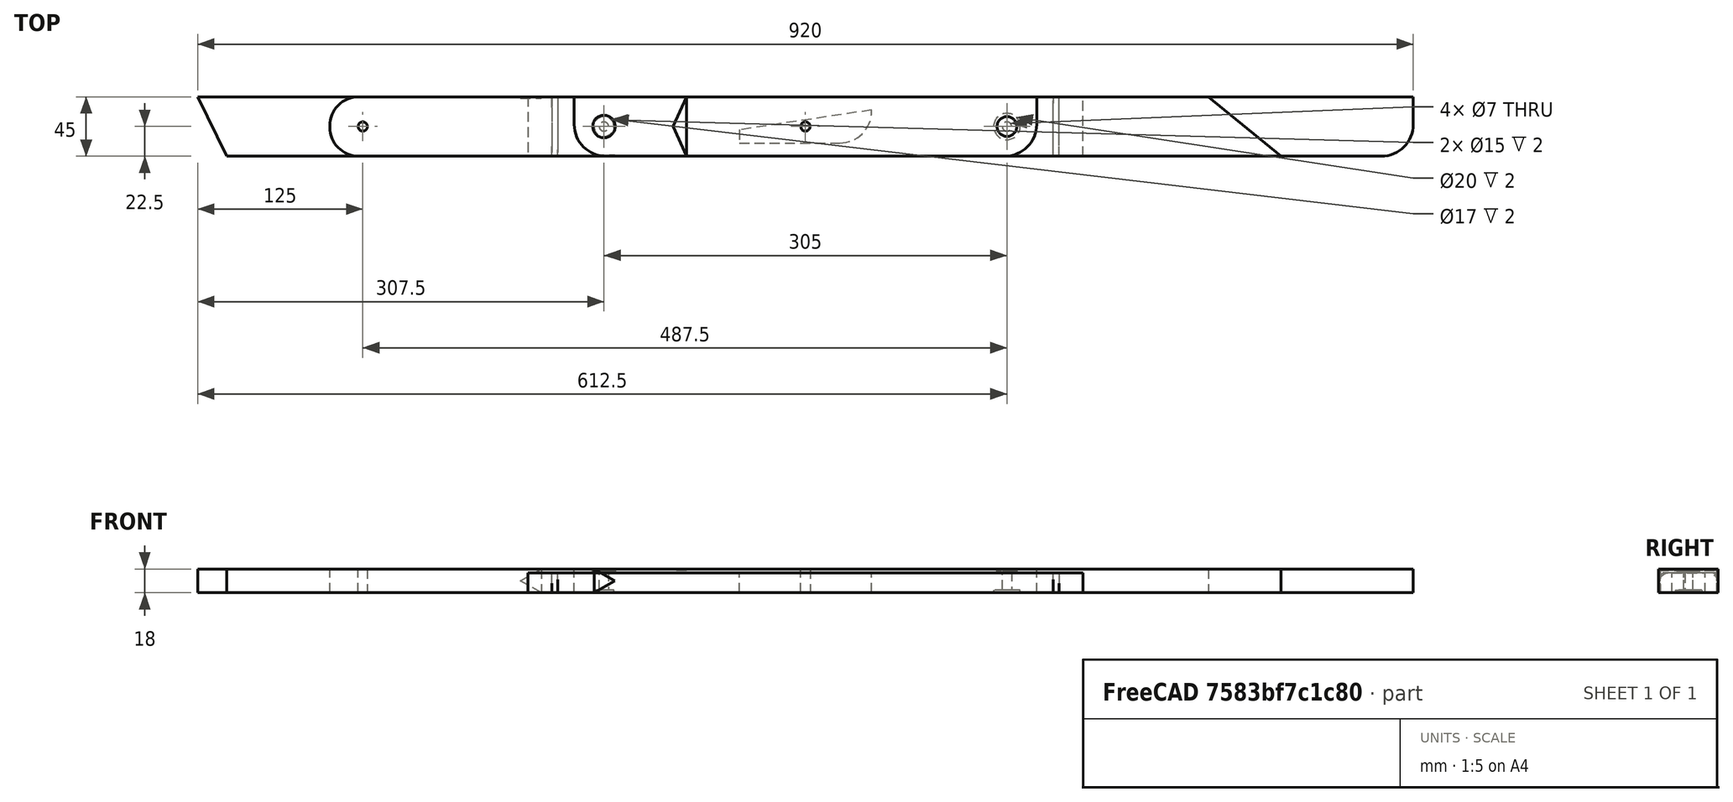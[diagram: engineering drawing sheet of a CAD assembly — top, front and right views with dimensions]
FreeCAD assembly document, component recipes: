
FREECAD ASSEMBLY — COMPONENT RECIPES ("wooden folding chair")

This assembly document has 20 components, labeled P0..P19 below (a component is one placed body or linked part). 20 of them carry a construction recipe — the FreeCAD feature program that regenerates the part from scratch, quoted from this document or its linked companion documents; the rest are supplied as boundary geometry only. No exploded tour is included for this assembly.
COMPONENT P0 — recipe-attached ("35 X 4,5 X 1,8 (1)", modeled in this document).
Construction recipe (the document's own serialized feature program — sketch geometry with constraints, then the solid features built on it; lengths are millimeters unless a unit is written):

FEATURE [Sketcher::SketchObject] Sketch
  FullyConstrained = true
  MapMode = 5
  Support = -> [XY_Plane]
  sketch-geometry (5):
    g0: LineSegment StartX=-175 StartY=22.5 StartZ=0 EndX=-175 EndY=-22.5 EndZ=0
    g1: LineSegment StartX=-175 StartY=-22.5 StartZ=0 EndX=175 EndY=-22.5 EndZ=0
    g2: LineSegment StartX=175 StartY=-22.5 StartZ=0 EndX=175 EndY=22.5 EndZ=0
    g3: LineSegment StartX=175 StartY=22.5 StartZ=0 EndX=-175 EndY=22.5 EndZ=0
    g4: GeomPoint X=0 Y=0 Z=0
  constraints (12):
    c: Coincident(g0,g1)
    c: Coincident(g1,g2)
    c: Coincident(g2,g3)
    c: Coincident(g3,g0)
    c: Horizontal(g1)
    c: Horizontal(g3)
    c: Vertical(g0)
    c: Vertical(g2)
    c: Symmetric(g1,g0,g4)
    c: Coincident(g4,g-1)
    c: DistanceY(g0,g0) = 45
    c: DistanceX(g3,g3) = 350
FEATURE [PartDesign::Pad] Pad
  Direction = (0,0,1)
  Length = 18
  Length2 = 10
  Profile = -> Sketch
  ReferenceAxis = -> Sketch [N_Axis]
  Type = 0
FEATURE [Sketcher::SketchObject] Sketch001
  ExternalGeometry = -> [Pad]
  FullyConstrained = true
  MapMode = 5
  Placement = pos=(0,0,18) rot=(0,0,1;0rad)
  Support = -> [Pad]
  sketch-geometry (2):
    g0: Circle CenterX=-152.5 CenterY=0 CenterZ=0 NormalX=0 NormalY=0 NormalZ=1 AngleXU=0 Radius=3.5
    g1: Circle CenterX=-152.5 CenterY=0 CenterZ=0 NormalX=0 NormalY=0 NormalZ=1 AngleXU=0 Radius=8.5
  constraints (5):
    c: PointOnObject(g0,g-1)
    c: Diameter(g0) = 7
    c: DistanceX(g-3,g0) = 22.5
    c: Coincident(g1,g0)
    c: Diameter(g1) = 17
FEATURE [PartDesign::Pocket] Pocket
  BaseFeature = -> Pad
  Direction = (0,0,-1)
  Length = 2
  Length2 = 5
  Profile = -> Sketch001
  ReferenceAxis = -> Sketch001 [N_Axis]
  Type = 0
FEATURE [PartDesign::Pocket] Pocket001
  BaseFeature = -> Pocket
  Direction = (0,0,-1)
  Length = 5
  Length2 = 5
  Profile = -> Pocket [Edge18]
  Type = 1
FEATURE [PartDesign::LinearPattern] LinearPattern
  BaseFeature = -> Pocket001
  Direction = -> X_Axis
  Length = 305
  Occurrences = 2
  Originals = -> [Pocket001]
FEATURE [Sketcher::SketchObject] Sketch002
  ExternalGeometry = -> [LinearPattern]
  FullyConstrained = true
  MapMode = 5
  Placement = pos=(0,0,0) rot=(1,0,0;3.14159rad)
  Support = -> [LinearPattern]
  sketch-geometry (1):
    g0: Circle CenterX=152.5 CenterY=0 CenterZ=0 NormalX=0 NormalY=0 NormalZ=1 AngleXU=0 Radius=10
  constraints (2):
    c: Coincident(g0,g-3)
    c: Diameter(g0) = 20
FEATURE [PartDesign::Pocket] Pocket002
  BaseFeature = -> LinearPattern
  Direction = (0,0,1)
  Length = 2
  Length2 = 5
  Profile = -> Sketch002
  ReferenceAxis = -> Sketch002 [N_Axis]
  Type = 0
FEATURE [PartDesign::Fillet] Fillet
  Base = -> Pocket002 [Edge2,Edge8]
  BaseFeature = -> Pocket002
  Radius = 24
  SupportTransform = false
  UseAllEdges = false
FEATURE [Sketcher::SketchObject] Sketch003
  ExternalGeometry = -> [Fillet]
  FullyConstrained = true
  MapMode = 5
  Placement = pos=(0,0,18) rot=(0,0,1;0rad)
  Support = -> [Fillet]
  sketch-geometry (1):
    g0: Circle CenterX=152.5 CenterY=0 CenterZ=0 NormalX=0 NormalY=0 NormalZ=1 AngleXU=0 Radius=7.5
  constraints (2):
    c: Coincident(g0,g-3)
    c: Diameter(g0) = 15
FEATURE [PartDesign::Pocket] Pocket003
  BaseFeature = -> Fillet
  Direction = (0,0,-1)
  Length = 2
  Length2 = 5
  Profile = -> Sketch003
  ReferenceAxis = -> Sketch003 [N_Axis]
  Type = 0
FEATURE [Sketcher::SketchObject] Sketch004
  ExternalGeometry = -> [Pocket003]
  FullyConstrained = true
  MapMode = 5
  Placement = pos=(0,0,0) rot=(1,0,0;3.14159rad)
  Support = -> [Pocket003]
  sketch-geometry (1):
    g0: Circle CenterX=-152.5 CenterY=0 CenterZ=0 NormalX=0 NormalY=0 NormalZ=1 AngleXU=0 Radius=7.5
  constraints (2):
    c: Coincident(g0,g-3)
    c: Diameter(g0) = 15
FEATURE [PartDesign::Pocket] Pocket004
  BaseFeature = -> Pocket003
  Direction = (0,0,1)
  Length = 2
  Length2 = 5
  Profile = -> Sketch004
  ReferenceAxis = -> Sketch004 [N_Axis]
  Type = 0
FEATURE [PartDesign::Body] Body  label="35 x 4,5 x 1,8"
  Group = -> [Sketch,Pad,Sketch001,Pocket,Pocket001,LinearPattern,Sketch002,Pocket002,Fillet,Sketch003,Pocket003,Sketch004,Pocket004]
  Origin = -> Origin
  Tip = -> Pocket004
COMPONENT P1 — recipe-attached ("37,5 X 4,5 X 1,5 (1)", modeled in this document).
Construction recipe (the document's own serialized feature program — sketch geometry with constraints, then the solid features built on it; lengths are millimeters unless a unit is written):

FEATURE [Sketcher::SketchObject] Sketch005
  FullyConstrained = true
  MapMode = 5
  Support = -> [XY_Plane001]
  sketch-geometry (5):
    g0: LineSegment StartX=-187.5 StartY=22.5 StartZ=0 EndX=-187.5 EndY=-22.5 EndZ=0
    g1: LineSegment StartX=-187.5 StartY=-22.5 StartZ=0 EndX=187.5 EndY=-22.5 EndZ=0
    g2: LineSegment StartX=187.5 StartY=-22.5 StartZ=0 EndX=187.5 EndY=22.5 EndZ=0
    g3: LineSegment StartX=187.5 StartY=22.5 StartZ=0 EndX=-187.5 EndY=22.5 EndZ=0
    g4: GeomPoint X=0 Y=0 Z=0
  constraints (12):
    c: Coincident(g0,g1)
    c: Coincident(g1,g2)
    c: Coincident(g2,g3)
    c: Coincident(g3,g0)
    c: Horizontal(g1)
    c: Horizontal(g3)
    c: Vertical(g0)
    c: Vertical(g2)
    c: Symmetric(g1,g0,g4)
    c: Coincident(g4,g-1)
    c: DistanceY(g0,g0) = 45
    c: DistanceX(g3,g3) = 375
FEATURE [PartDesign::Pad] Pad001
  Direction = (0,0,1)
  Length = 15
  Length2 = 10
  Profile = -> Sketch005
  ReferenceAxis = -> Sketch005 [N_Axis]
  Type = 0
FEATURE [PartDesign::Fillet] Fillet001
  Base = -> Pad001 [Edge7,Edge12]
  BaseFeature = -> Pad001
  Radius = 5
  SupportTransform = false
  UseAllEdges = false
FEATURE [PartDesign::Body] Body001  label="37,5 x 4,5 x 1,5"
  Group = -> [Sketch005,Pad001,Fillet001]
  Origin = -> Origin001
  Tip = -> Fillet001
COMPONENT P2 — same part as P1; its construction recipe is shown at P1.
COMPONENT P3 — same part as P0; its construction recipe is shown at P0.
COMPONENT P4 — same part as P1; its construction recipe is shown at P1.
COMPONENT P5 — same part as P1; its construction recipe is shown at P1.
COMPONENT P6 — same part as P1; its construction recipe is shown at P1.
COMPONENT P7 — same part as P1; its construction recipe is shown at P1.
COMPONENT P8 — same part as P1; its construction recipe is shown at P1.
COMPONENT P9 — recipe-attached ("pe1", modeled in this document).
Construction recipe (the document's own serialized feature program — sketch geometry with constraints, then the solid features built on it; lengths are millimeters unless a unit is written):

FEATURE [Sketcher::SketchObject] Sketch006
  FullyConstrained = true
  MapMode = 5
  Support = -> [XY_Plane002]
  sketch-geometry (5):
    g0: LineSegment StartX=-360 StartY=22.5 StartZ=0 EndX=-360 EndY=-22.5 EndZ=0
    g1: LineSegment StartX=-360 StartY=-22.5 StartZ=0 EndX=360 EndY=-22.5 EndZ=0
    g2: LineSegment StartX=360 StartY=-22.5 StartZ=0 EndX=360 EndY=22.5 EndZ=0
    g3: LineSegment StartX=360 StartY=22.5 StartZ=0 EndX=-360 EndY=22.5 EndZ=0
    g4: GeomPoint X=0 Y=0 Z=0
  constraints (12):
    c: Coincident(g0,g1)
    c: Coincident(g1,g2)
    c: Coincident(g2,g3)
    c: Coincident(g3,g0)
    c: Horizontal(g1)
    c: Horizontal(g3)
    c: Vertical(g0)
    c: Vertical(g2)
    c: Symmetric(g1,g0,g4)
    c: Coincident(g4,g-1)
    c: DistanceY(g2,g2) = 45
    c: DistanceX(g3,g3) = 720
FEATURE [PartDesign::Pad] Pad002
  Direction = (0,0,1)
  Length = 18
  Length2 = 10
  Profile = -> Sketch006
  ReferenceAxis = -> Sketch006 [N_Axis]
  Type = 0
FEATURE [Sketcher::SketchObject] Sketch007
  ExternalGeometry = -> [Pad002]
  FullyConstrained = true
  MapMode = 5
  Placement = pos=(0,0,18) rot=(0,0,1;0rad)
  Support = -> [Pad002]
  sketch-geometry (1):
    g0: Circle CenterX=-335 CenterY=0 CenterZ=0 NormalX=0 NormalY=0 NormalZ=1 AngleXU=0 Radius=3.5
  constraints (3):
    c: PointOnObject(g0,g-1)
    c: Diameter(g0) = 7
    c: DistanceX(g-3,g0) = 25
FEATURE [PartDesign::Pocket] Pocket006
  BaseFeature = -> Pad002
  Direction = (0,0,-1)
  Length = 5
  Length2 = 5
  Profile = -> Sketch007
  ReferenceAxis = -> Sketch007 [N_Axis]
  Type = 1
FEATURE [PartDesign::Fillet] Fillet002
  Base = -> Pocket006 [Edge2,Edge1]
  BaseFeature = -> Pocket006
  Radius = 22
  SupportTransform = false
  UseAllEdges = false
FEATURE [Sketcher::SketchObject] Sketch008
  ExternalGeometry = -> [Fillet002]
  FullyConstrained = true
  MapMode = 5
  Placement = pos=(0,0,18) rot=(0,0,1;0rad)
  Support = -> [Fillet002]
  sketch-geometry (3):
    g0: LineSegment StartX=-90 StartY=-22.5 StartZ=0 EndX=-90 EndY=22.5 EndZ=0
    g1: LineSegment StartX=-90 StartY=22.5 StartZ=0 EndX=-100 EndY=0 EndZ=0
    g2: LineSegment StartX=-100 StartY=0 StartZ=0 EndX=-90 EndY=-22.5 EndZ=0
  constraints (9):
    c: PointOnObject(g0,g-3)
    c: PointOnObject(g0,g-4)
    c: Vertical(g0)
    c: Coincident(g0,g1)
    c: PointOnObject(g1,g-1)
    c: Coincident(g1,g2)
    c: Coincident(g2,g0)
    c: DistanceX(g-5,g0) = 270
    c: DistanceX(g1,g0) = 10
FEATURE [PartDesign::Pocket] Pocket007
  BaseFeature = -> Fillet002
  Direction = (0,0,-1)
  Length = 1
  Length2 = 5
  Profile = -> Sketch008
  ReferenceAxis = -> Sketch008 [N_Axis]
  Type = 0
FEATURE [Sketcher::SketchObject] Sketch009
  ExternalGeometry = -> [Pocket007]
  FullyConstrained = true
  MapMode = 5
  Placement = pos=(0,0,18) rot=(0,0,1;0rad)
  Support = -> [Pocket007]
  sketch-geometry (3):
    g0: LineSegment StartX=360 StartY=22.5 StartZ=0 EndX=305 EndY=22.5 EndZ=0
    g1: LineSegment StartX=305 StartY=22.5 StartZ=0 EndX=360 EndY=-22.5 EndZ=0
    g2: LineSegment StartX=360 StartY=22.5 StartZ=0 EndX=360 EndY=-22.5 EndZ=0
  constraints (7):
    c: Coincident(g-4,g0)
    c: PointOnObject(g0,g-3)
    c: Coincident(g0,g1)
    c: Coincident(g1,g-4)
    c: DistanceX(g0,g0) = 55
    c: Coincident(g2,g0)
    c: Coincident(g2,g1)
FEATURE [PartDesign::Pocket] Pocket005
  BaseFeature = -> Pocket007
  Direction = (0,0,-1)
  Length = 5
  Length2 = 5
  Profile = -> Sketch009
  ReferenceAxis = -> Sketch009 [N_Axis]
  Type = 1
FEATURE [PartDesign::Body] Body002  label="72 x 4,5 x 1,8"
  Group = -> [Sketch006,Pad002,Sketch007,Pocket006,Fillet002,Sketch008,Pocket007,Sketch009,Pocket005]
  Origin = -> Origin002
  Tip = -> Pocket005
COMPONENT P10 — same part as P9; its construction recipe is shown at P9.
COMPONENT P11 — same part as P1; its construction recipe is shown at P1.
COMPONENT P12 — recipe-attached ("92 X 4,5 X 1,8 (1)", modeled in this document).
Construction recipe (the document's own serialized feature program — sketch geometry with constraints, then the solid features built on it; lengths are millimeters unless a unit is written):

FEATURE [Sketcher::SketchObject] Sketch010
  FullyConstrained = true
  MapMode = 5
  Support = -> [XY_Plane003]
  sketch-geometry (5):
    g0: LineSegment StartX=-460 StartY=22.5 StartZ=0 EndX=-460 EndY=-22.5 EndZ=0
    g1: LineSegment StartX=-460 StartY=-22.5 StartZ=0 EndX=460 EndY=-22.5 EndZ=0
    g2: LineSegment StartX=460 StartY=-22.5 StartZ=0 EndX=460 EndY=22.5 EndZ=0
    g3: LineSegment StartX=460 StartY=22.5 StartZ=0 EndX=-460 EndY=22.5 EndZ=0
    g4: GeomPoint X=0 Y=0 Z=0
  constraints (12):
    c: Coincident(g0,g1)
    c: Coincident(g1,g2)
    c: Coincident(g2,g3)
    c: Coincident(g3,g0)
    c: Horizontal(g1)
    c: Horizontal(g3)
    c: Vertical(g0)
    c: Vertical(g2)
    c: Symmetric(g1,g0,g4)
    c: Coincident(g4,g-1)
    c: DistanceY(g2,g2) = 45
    c: DistanceX(g3,g3) = 920
FEATURE [PartDesign::Pad] Pad003
  Direction = (0,0,1)
  Length = 18
  Length2 = 10
  Profile = -> Sketch010
  ReferenceAxis = -> Sketch010 [N_Axis]
  Type = 0
FEATURE [Sketcher::SketchObject] Sketch011
  FullyConstrained = true
  MapMode = 5
  Placement = pos=(0,0,18) rot=(0,0,1;0rad)
  Support = -> [Pad003]
  sketch-geometry (1):
    g0: Circle CenterX=0 CenterY=0 CenterZ=0 NormalX=0 NormalY=0 NormalZ=1 AngleXU=0 Radius=3.5
  constraints (2):
    c: Coincident(g0,g-1)
    c: Diameter(g0) = 7
FEATURE [PartDesign::Pocket] Pocket009
  BaseFeature = -> Pad003
  Direction = (0,0,-1)
  Length = 5
  Length2 = 5
  Profile = -> Sketch011
  ReferenceAxis = -> Sketch011 [N_Axis]
  Type = 1
FEATURE [PartDesign::Fillet] Fillet003
  Base = -> Pocket009 [Edge8]
  BaseFeature = -> Pocket009
  Radius = 24
  SupportTransform = false
  UseAllEdges = false
FEATURE [Sketcher::SketchObject] Sketch012
  ExternalGeometry = -> [Fillet003]
  FullyConstrained = true
  MapMode = 5
  Placement = pos=(0,-22.5,0) rot=(1,0,0;1.5708rad)
  Support = -> [Fillet003]
  sketch-geometry (3):
    g0: LineSegment StartX=-160 StartY=18 StartZ=0 EndX=-160 EndY=0 EndZ=0
    g1: LineSegment StartX=-160 StartY=0 StartZ=0 EndX=-144.412 EndY=9 EndZ=0
    g2: LineSegment StartX=-144.412 StartY=9 StartZ=0 EndX=-160 EndY=18 EndZ=0
  constraints (9):
    c: PointOnObject(g0,g-3)
    c: PointOnObject(g0,g-4)
    c: Vertical(g0)
    c: DistanceX(g-3,g0) = 300
    c: Coincident(g0,g1)
    c: Coincident(g1,g2)
    c: Coincident(g2,g0)
    c: Equal(g2,g1)
    c: Equal(g0,g1)
FEATURE [PartDesign::Pocket] Pocket010
  BaseFeature = -> Fillet003
  Direction = (0,1,-2e-16)
  Length = 1
  Length2 = 5
  Profile = -> Sketch012
  ReferenceAxis = -> Sketch012 [N_Axis]
  Type = 0
FEATURE [Sketcher::SketchObject] Sketch013
  ExternalGeometry = -> [Pocket010]
  FullyConstrained = true
  MapMode = 5
  Placement = pos=(0,22.5,0) rot=(0,0.707107,0.707107;3.14159rad)
  Support = -> [Pocket010]
  sketch-geometry (3):
    g0: LineSegment StartX=200 StartY=18 StartZ=0 EndX=200 EndY=0 EndZ=0
    g1: LineSegment StartX=200 StartY=0 StartZ=0 EndX=215.588 EndY=9 EndZ=0
    g2: LineSegment StartX=215.588 StartY=9 StartZ=0 EndX=200 EndY=18 EndZ=0
  constraints (9):
    c: PointOnObject(g0,g-3)
    c: PointOnObject(g0,g-4)
    c: Vertical(g0)
    c: Coincident(g0,g1)
    c: Coincident(g1,g2)
    c: Coincident(g2,g0)
    c: Equal(g0,g2)
    c: Equal(g2,g1)
    c: DistanceX(g0,g-3) = 260
FEATURE [PartDesign::Pocket] Pocket011
  BaseFeature = -> Pocket010
  Direction = (0,-1,2e-16)
  Length = 1
  Length2 = 5
  Profile = -> Sketch013
  ReferenceAxis = -> Sketch013 [N_Axis]
  Type = 0
FEATURE [Sketcher::SketchObject] Sketch014
  ExternalGeometry = -> [Pocket011]
  FullyConstrained = true
  MapMode = 5
  Placement = pos=(0,0,18) rot=(0,0,1;0rad)
  Support = -> [Pocket011]
  sketch-geometry (3):
    g0: LineSegment StartX=-460 StartY=-22.5 StartZ=0 EndX=-438 EndY=-22.5 EndZ=0
    g1: LineSegment StartX=-438 StartY=-22.5 StartZ=0 EndX=-460 EndY=22.5 EndZ=0
    g2: LineSegment StartX=-460 StartY=22.5 StartZ=0 EndX=-460 EndY=-22.5 EndZ=0
  constraints (7):
    c: Coincident(g-3,g0)
    c: PointOnObject(g0,g-3)
    c: Coincident(g0,g1)
    c: Coincident(g1,g-4)
    c: Coincident(g1,g2)
    c: Coincident(g2,g0)
    c: DistanceX(g0,g0) = 22
FEATURE [PartDesign::Pocket] Pocket008
  BaseFeature = -> Pocket011
  Direction = (0,0,-1)
  Length = 5
  Length2 = 5
  Profile = -> Sketch014
  ReferenceAxis = -> Sketch014 [N_Axis]
  Type = 1
FEATURE [PartDesign::Body] Body003  label="92 x 4,5 x 1,8"
  Group = -> [Sketch010,Pad003,Sketch011,Pocket009,Fillet003,Sketch012,Pocket010,Sketch013,Pocket011,Sketch014,Pocket008]
  Origin = -> Origin003
  Tip = -> Pocket008
COMPONENT P13 — recipe-attached ("42 X 4,5 X 1,5 (1)", modeled in this document).
Construction recipe (the document's own serialized feature program — sketch geometry with constraints, then the solid features built on it; lengths are millimeters unless a unit is written):

FEATURE [Sketcher::SketchObject] Sketch015
  FullyConstrained = true
  MapMode = 5
  Support = -> [XY_Plane004]
  sketch-geometry (5):
    g0: LineSegment StartX=-210 StartY=22.5 StartZ=0 EndX=-210 EndY=-22.5 EndZ=0
    g1: LineSegment StartX=-210 StartY=-22.5 StartZ=0 EndX=210 EndY=-22.5 EndZ=0
    g2: LineSegment StartX=210 StartY=-22.5 StartZ=0 EndX=210 EndY=22.5 EndZ=0
    g3: LineSegment StartX=210 StartY=22.5 StartZ=0 EndX=-210 EndY=22.5 EndZ=0
    g4: GeomPoint X=0 Y=0 Z=0
  constraints (12):
    c: Coincident(g0,g1)
    c: Coincident(g1,g2)
    c: Coincident(g2,g3)
    c: Coincident(g3,g0)
    c: Horizontal(g1)
    c: Horizontal(g3)
    c: Vertical(g0)
    c: Vertical(g2)
    c: Symmetric(g1,g0,g4)
    c: Coincident(g4,g-1)
    c: DistanceY(g0,g0) = 45
    c: DistanceX(g3,g3) = 420
FEATURE [PartDesign::Pad] Pad004
  Direction = (0,0,1)
  Length = 15
  Length2 = 10
  Profile = -> Sketch015
  ReferenceAxis = -> Sketch015 [N_Axis]
  Type = 0
FEATURE [PartDesign::Body] Body004  label="42 x 4,5 x 1,5"
  Group = -> [Sketch015,Pad004]
  Origin = -> Origin004
  Tip = -> Pad004
COMPONENT P14 — same part as P12; its construction recipe is shown at P12.
COMPONENT P15 — same part as P13; its construction recipe is shown at P13.
COMPONENT P16 — recipe-attached ("p7 (1)", modeled in this document).
Construction recipe (the document's own serialized feature program — sketch geometry with constraints, then the solid features built on it; lengths are millimeters unless a unit is written):

FEATURE [Sketcher::SketchObject] Sketch016
  FullyConstrained = true
  MapMode = 5
  Support = -> [XY_Plane005]
  sketch-geometry (5):
    g0: LineSegment StartX=-50 StartY=12.5 StartZ=0 EndX=-50 EndY=-12.5 EndZ=0
    g1: LineSegment StartX=-50 StartY=-12.5 StartZ=0 EndX=50 EndY=-12.5 EndZ=0
    g2: LineSegment StartX=50 StartY=-12.5 StartZ=0 EndX=50 EndY=12.5 EndZ=0
    g3: LineSegment StartX=50 StartY=12.5 StartZ=0 EndX=-50 EndY=12.5 EndZ=0
    g4: GeomPoint X=0 Y=0 Z=0
  constraints (12):
    c: Coincident(g0,g1)
    c: Coincident(g1,g2)
    c: Coincident(g2,g3)
    c: Coincident(g3,g0)
    c: Horizontal(g1)
    c: Horizontal(g3)
    c: Vertical(g0)
    c: Vertical(g2)
    c: Symmetric(g1,g0,g4)
    c: Coincident(g4,g-1)
    c: DistanceX(g3,g3) = 100
    c: DistanceY(g0,g0) = 25
FEATURE [PartDesign::Pad] Pad005
  Direction = (0,0,1)
  Length = 15
  Length2 = 10
  Profile = -> Sketch016
  ReferenceAxis = -> Sketch016 [N_Axis]
  Type = 0
FEATURE [PartDesign::Fillet] Fillet004
  Base = -> Pad005 [Edge5]
  BaseFeature = -> Pad005
  Radius = 24
  SupportTransform = false
  UseAllEdges = false
FEATURE [Sketcher::SketchObject] Sketch017
  ExternalGeometry = -> [Fillet004]
  FullyConstrained = true
  MapMode = 5
  Placement = pos=(0,0,15) rot=(0,0,1;0rad)
  Support = -> [Fillet004]
  sketch-geometry (3):
    g0: LineSegment StartX=50 StartY=12.5 StartZ=0 EndX=-50 EndY=-2.5 EndZ=0
    g1: LineSegment StartX=-50 StartY=-2.5 StartZ=0 EndX=-50 EndY=12.5 EndZ=0
    g2: LineSegment StartX=-50 StartY=12.5 StartZ=0 EndX=50 EndY=12.5 EndZ=0
  constraints (7):
    c: Coincident(g-3,g0)
    c: Coincident(g0,g1)
    c: Coincident(g1,g-3)
    c: Vertical(g1)
    c: Coincident(g1,g2)
    c: Coincident(g2,g0)
    c: DistanceY(g1,g1) = 15
FEATURE [PartDesign::Pocket] Pocket012
  BaseFeature = -> Fillet004
  Direction = (0,0,-1)
  Length = 5
  Length2 = 5
  Profile = -> Sketch017
  ReferenceAxis = -> Sketch017 [N_Axis]
  Type = 1
FEATURE [PartDesign::Body] Body005  label="Anteparo"
  Group = -> [Sketch016,Pad005,Fillet004,Sketch017,Pocket012]
  Origin = -> Origin005
  Tip = -> Pocket012
COMPONENT P17 — same part as P16; its construction recipe is shown at P16.
COMPONENT P18 — recipe-attached ("38,4 X 4,5 X 1,5 (1)", modeled in this document).
Construction recipe (the document's own serialized feature program — sketch geometry with constraints, then the solid features built on it; lengths are millimeters unless a unit is written):

FEATURE [Sketcher::SketchObject] Sketch018
  FullyConstrained = true
  MapMode = 5
  Support = -> [XY_Plane006]
  sketch-geometry (5):
    g0: LineSegment StartX=-192 StartY=22.5 StartZ=0 EndX=-192 EndY=-22.5 EndZ=0
    g1: LineSegment StartX=-192 StartY=-22.5 StartZ=0 EndX=192 EndY=-22.5 EndZ=0
    g2: LineSegment StartX=192 StartY=-22.5 StartZ=0 EndX=192 EndY=22.5 EndZ=0
    g3: LineSegment StartX=192 StartY=22.5 StartZ=0 EndX=-192 EndY=22.5 EndZ=0
    g4: GeomPoint X=0 Y=0 Z=0
  constraints (12):
    c: Coincident(g0,g1)
    c: Coincident(g1,g2)
    c: Coincident(g2,g3)
    c: Coincident(g3,g0)
    c: Horizontal(g1)
    c: Horizontal(g3)
    c: Vertical(g0)
    c: Vertical(g2)
    c: Symmetric(g1,g0,g4)
    c: Coincident(g4,g-1)
    c: DistanceY(g0,g0) = 45
    c: DistanceX(g3,g3) = 384
FEATURE [PartDesign::Pad] Pad006
  Direction = (0,0,1)
  Length = 15
  Length2 = 10
  Profile = -> Sketch018
  ReferenceAxis = -> Sketch018 [N_Axis]
  Type = 0
FEATURE [PartDesign::Fillet] Fillet006
  Base = -> Pad006 [Edge7]
  BaseFeature = -> Pad006
  Radius = 8
  SupportTransform = false
  UseAllEdges = false
FEATURE [PartDesign::Fillet] Fillet005
  Base = -> Fillet006 [Edge13]
  BaseFeature = -> Fillet006
  Radius = 8
  SupportTransform = false
  UseAllEdges = false
FEATURE [PartDesign::Body] Body006  label="38,4 X 4,5 X 1,5"
  Group = -> [Sketch018,Pad006,Fillet006,Fillet005]
  Origin = -> Origin006
  Tip = -> Fillet005
COMPONENT P19 — same part as P18; its construction recipe is shown at P18.
PROVENANCE & LICENSES
A FreeCAD (.FCStd) document from a public repository crawl; recipes are the document's own serialized feature recipes (and, for linked parts, companion documents' recipes).
License: mit.
